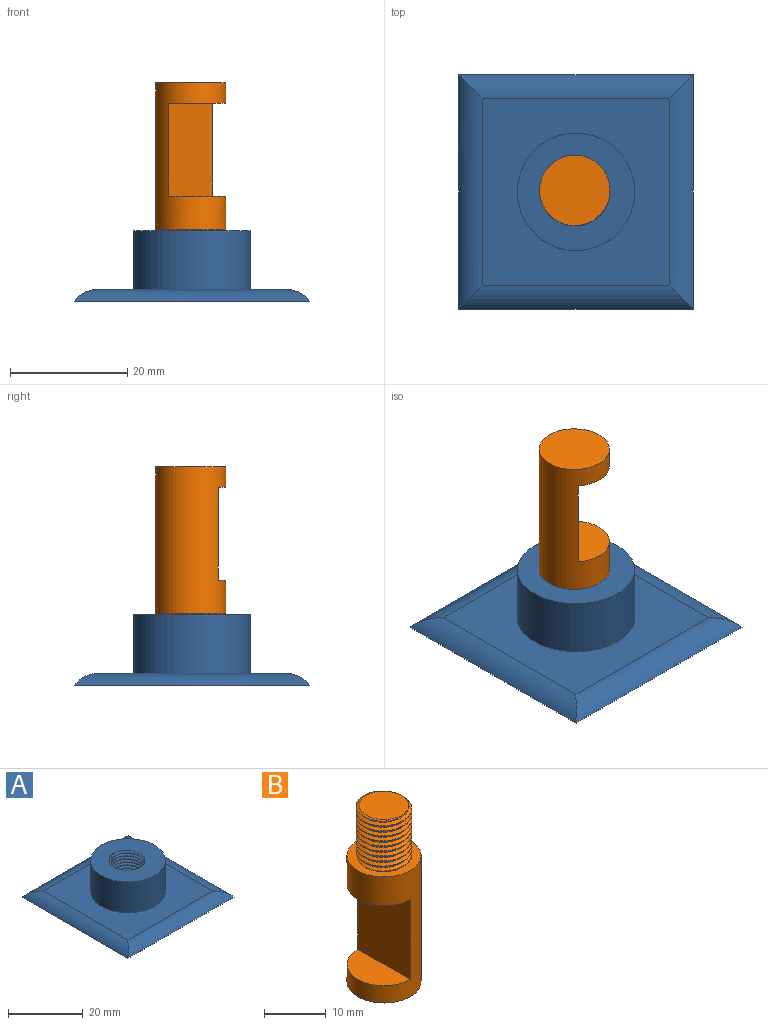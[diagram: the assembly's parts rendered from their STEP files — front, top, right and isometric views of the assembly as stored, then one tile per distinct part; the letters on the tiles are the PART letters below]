
ASSEMBLY  parts=2 mates=1
PART A: 12 faces, bbox 40.3x40.3x13.1 mm
  f0: plane 40.3x40.3mm, normal (0,0,-1), area 1529.3mm2, adj f3,f4,f5,f6,f8,f9,f10,f11
  f1: plane 20.3x20.3mm, normal (0,0,1), area 243.5mm2, adj f7,f8,f9,f10,f11
  f2: plane 32x32mm, normal (0,0,1), area 709.8mm2, adj f3,f4,f5,f6,f7
  f3: cylinder r=5mm len=40mm, axis (0,-1,0), area 166.9mm2, adj f0,f2,f4,f5
  f4: cylinder r=5mm len=40mm, axis (1,0,0), area 166.9mm2, adj f0,f2,f3,f6
  f5: cylinder r=5mm len=40mm, axis (-1,0,0), area 166.9mm2, adj f0,f2,f3,f6
  f6: cylinder r=5mm len=40mm, axis (0,1,0), area 166.9mm2, adj f0,f2,f4,f5
  f7: cylinder r=10mm len=20mm, axis (0,0,-1), area 628.3mm2, adj f1,f2
  f8: bspline ~12.65x11.64mm, area 225.4mm2, adj f0,f1,f10,f11
  f9: bspline ~12.81x11.64mm, area 224.5mm2, adj f0,f1,f10,f11
  f10: bspline ~12.46x11.75mm, area 55.4mm2, adj f0,f1,f8,f9
  f11: cylinder r=4.5mm len=12mm, axis (0,0,-1), area 58.9mm2, adj f0,f1,f8,f9
PART B: 12 faces, bbox 12.3x12.3x35.7 mm
  f0: cylinder r=4.51mm len=9.75mm, axis (0,0,-1), area 26.1mm2, adj f2,f9,f10,f11
  f1: cylinder r=6mm len=25mm, axis (0,0,-1), area 643.9mm2, adj f2,f3,f5,f6,f7
  f2: plane 12.29x12.29mm, normal (0,0,1), area 57.6mm2, adj f0,f1,f8,f9,f10
  f3: plane 12x12mm, normal (0,0,-1), area 113.1mm2, adj f1
  f4: plane 8.08x8mm, normal (0,0,1), area 50.1mm2, adj f8,f9,f10,f11
  f5: plane 15.84x12mm, normal (-1,0,0), area 190.1mm2, adj f1,f6,f7
  f6: plane 12x6mm, normal (0,0,-1), area 56.5mm2, adj f1,f5
  f7: plane 12x6mm, normal (0,0,1), area 56.5mm2, adj f1,f5
  f8: bspline ~10.75x9.17mm, area 69.3mm2, adj f2,f4,f9,f10
  f9: bspline ~10.81x10.42mm, area 164.3mm2, adj f0,f2,f4,f8,f11
  f10: bspline ~10.48x10.42mm, area 164.7mm2, adj f0,f2,f4,f8,f11
  f11: cone r=4.51mm half-angle=63.4deg, axis (0,0,-1), area 6.1mm2, adj f0,f4,f9,f10
PLACE A at identity fixed
PLACE B rot(axis=(-0.33,-0.94,0),180deg) t=(-0.21,0.21,37.16)mm
MATE cylindrical B.f0 <-> A.f1  axis (0,0,-1) through (-0.21,0.21,2.16)mm
